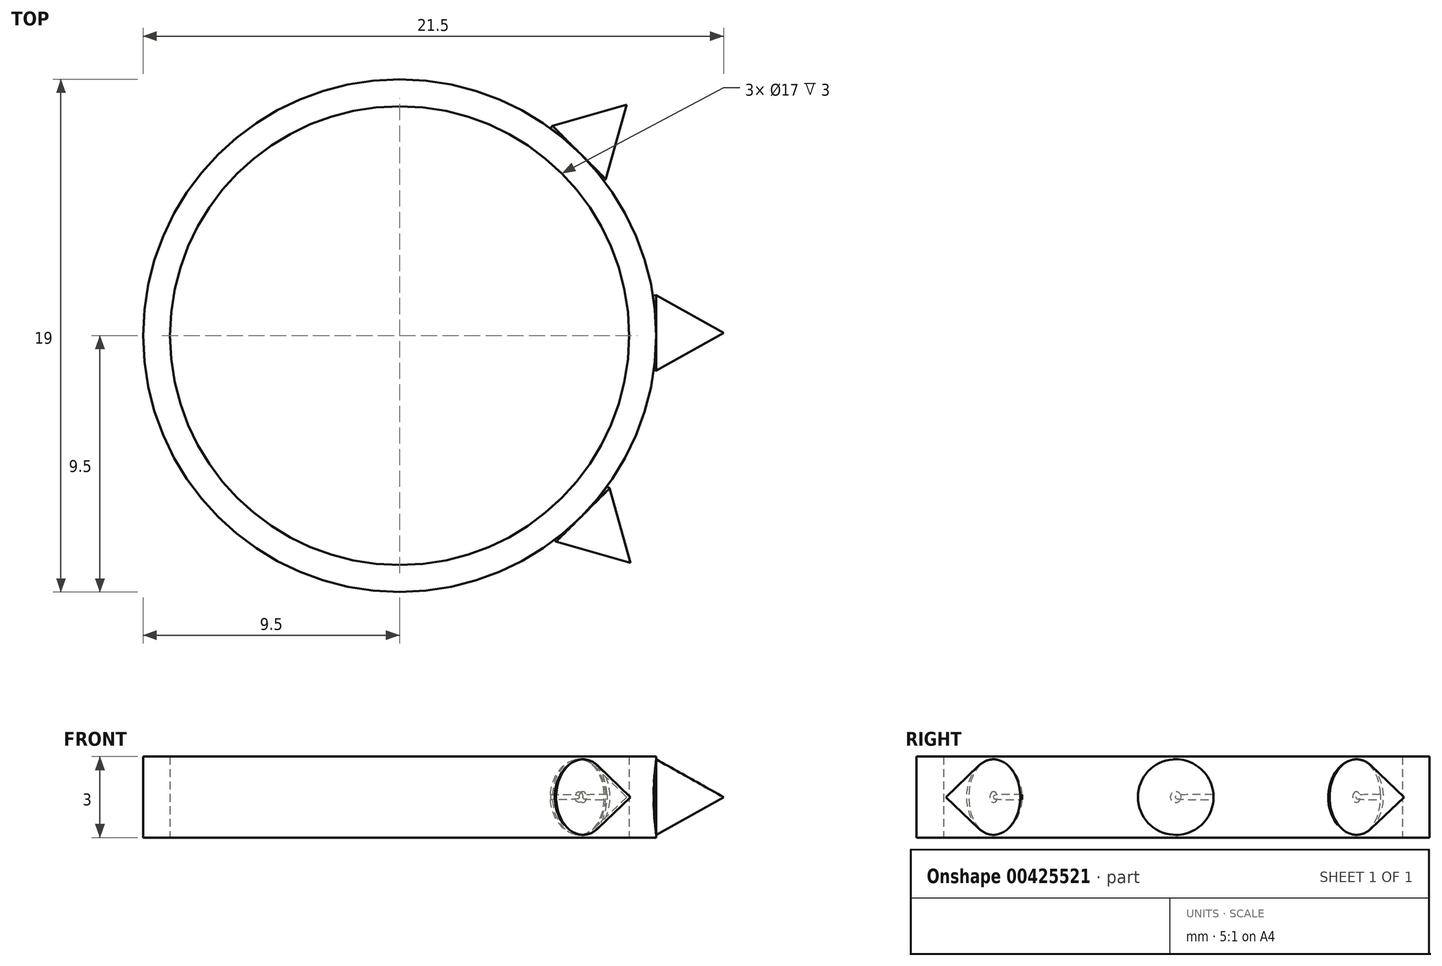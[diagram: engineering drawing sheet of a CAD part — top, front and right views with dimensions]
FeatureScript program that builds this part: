
annotation { "Feature Type Name" : "Feature", "Feature Type Description" : "" }
export const myFeature = defineFeature(function(context is Context, id is Id, definition is map)
    precondition{}
    {
        {
            var Q0;
            Q0=qCreatedBy(makeId("Top.planeOp"),FACE);
            var sketch = newSketch(context, id + "F0", { "sketchPlane" : qUnion([Q0])});
            skCircle(sketch, "E0", {"center": v(0, 0) * mm, "radius": 8.5 * mm});
            skCircle(sketch, "E1", {"center": v(0, 0) * mm, "radius": 9.5 * mm});
            skSolve(sketch);
        }
        {
            var Q0;
            Q0=makeQuery(id+"F0.imprint","IMPRINT",FACE,{"disambiguationData":[TD([[makeQuery(id+"F0.imprint","IMPRINT",EDGE,{"derivedFrom":sQuery(id+"F0.wireOp",EDGE,"E0")}),-1.0]])]});
            extrude(context, id + "F1", {"entities" : qUnion([Q0]), "depth" : 1.5 * mm, "hasSecondDirection" : true, "secondDirectionOppositeDirection" : true, "secondDirectionDepth" : 1.5 * mm});
        }
        {
            var Q0;
            Q0=qCreatedBy(makeId("Top.planeOp"),FACE);
            var sketch = newSketch(context, id + "F2", { "sketchPlane" : qUnion([Q0])});
            skLineSegment(sketch, "E2.right", {"start": v(9.5, 0.1) * mm, "end": v(9.5, 1.5) * mm});
            skLineSegment(sketch, "E3", {"start": v(9.5, 0.1) * mm, "end": v(12, 0.1) * mm});
            skLineSegment(sketch, "E4", {"start": v(12, 0.1) * mm, "end": v(9.5, 1.5) * mm});
            skArc(sketch, "E5", {"start": v(9.5, 0.1) * mm, "mid": v(9.47, 0.8) * mm, "end": v(9.38, 1.48) * mm});
            skLineSegment(sketch, "E6", {"start": v(9.5, 1.5) * mm, "end": v(9.38, 1.48) * mm});
            skSolve(sketch);
        }
        {
            var Q0;
            Q0 = qSketchRegion(id + "F2", true);
            var Q1;
            Q1=sQuery(id+"F2.wireOp",EDGE,"E3");
            revolve(context, id + "F3", {"operationType" : NewBodyOperationType.ADD, "entities" : qUnion([Q0]), "axis" : qUnion([Q1]), "revolveType" : RevolveType.FULL});
        }
        {
            var Q0;
            Q0=qCreatedBy(makeId("Front.planeOp"),FACE);
            var sketch = newSketch(context, id + "F4", { "sketchPlane" : qUnion([Q0])});
            skLineSegment(sketch, "E7", {"start": v(0, 11.23) * mm, "end": v(0, -8.15) * mm});
            skSolve(sketch);
        }
        {
            var Q0;
            Q0=makeQuery(id+"F1.opExtrude","SWEPT_BODY",BODY,{"disambiguationData":[OSD([sQuery(id+"F0.wireOp",EDGE,"E0"),sQuery(id+"F0.wireOp",EDGE,"E1")])]});
            var Q1;
            Q1=sQuery(id+"F4.wireOp",EDGE,"E7");
            circularPattern(context, id + "F5", {"entities" : qUnion([Q0]), "axis" : qUnion([Q1]), "angle" : 45 * degree, "instanceCount" : 2, "equalSpace" : true, "isCentered" : true});
        }
    });
